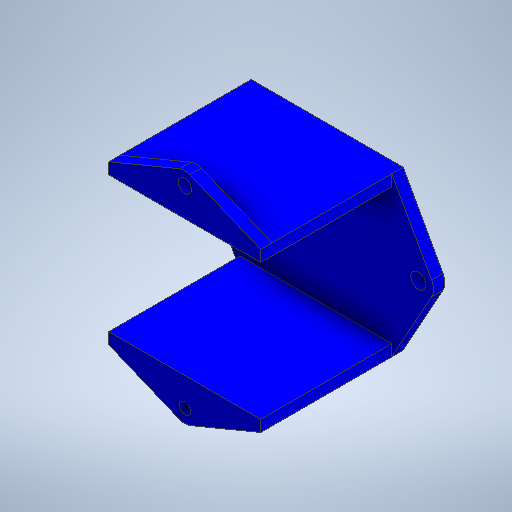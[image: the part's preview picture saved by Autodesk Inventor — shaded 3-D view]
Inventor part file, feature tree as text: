
AUTODESK INVENTOR PART (.ipt)
format: ipt  version: 2025.2 (Build 292293000, 293)  size: 303,616 bytes
history: native  units: mm
features: extrude x3, sketch x2
ambient origin geometry x8: Origin, YZ Plane, XZ Plane, XY Plane, X Axis, Y Axis, Z Axis, Center Point
bodies: Solid1 (feature_tree)
feature tree (5):
  sketch  "Sketch1"  dims[d0=3.5mm d1=50.75mm]
  extrude  "Extrusion1"  Depth=50.75mm
  extrude  "Extrusion2"  Depth=3.0mm
  extrude  "Extrusion3"  Depth=3.0mm
  sketch  "Sketch2"  dims[d2=3.0mm d3=7.5mm d4=3.0mm d5=40.0mm d6=40.0mm d7=7.0mm d8=7.5mm d9=3.0mm d10=40.0mm d11=40.0mm d12=7.0mm d13=3.0mm d14=0.0mm d15=31.5mm d16=0.0mm d17=17.875mm d18=54.0mm d19=8.0mm d20=4.0mm d21=8.0mm d22=4.0mm d23=3.0mm d24=0.0mm]
